# Revit family: 152-MM DUCHA EMPOTRADO KINGSLEY
name_source: partatom
category: Aparatos sanitarios
units: mm (PartAtom-declared; Revit-internal decimal feet)

## family parameters
Anfitrión = Muro
Compartido = Sí
Corte con vacíos al cargar = Sí
Cota de conector redondo = Diámetro de uso
Número OmniClass = 23.45.00.00
Punto de cálculo de habitación = No
Siempre vertical = Sí
Tipo de pieza = Normal
Título OmniClass = Sanitary, Laundry, and Cleaning Equipment

## types (1)
- MM DUCHA EMPOTRADO KINGSLEY
    Elevación por defecto = 90 cm
    F_Alto = 19 cm
    F_Ancho = 13 cm
    F_Color = Latón cromado
    F_Descripción = Grifería empotrada para ducha
    F_Distancia de instalación a muro terminado = 0 cm
    F_Peso = 0 kgf
    F_Productos necesarios para instalación = Rociador o plato de ducha, brazo de muro o techo o sistema de toma de agua con flexible
    F_Profundidad = 0 cm
    F_SKU = SGDE65393061CB
    F_Tipo de instalación = A muro
    Nota clave = Falta parte trasera empotrada
    URL = https://briggs.cl
